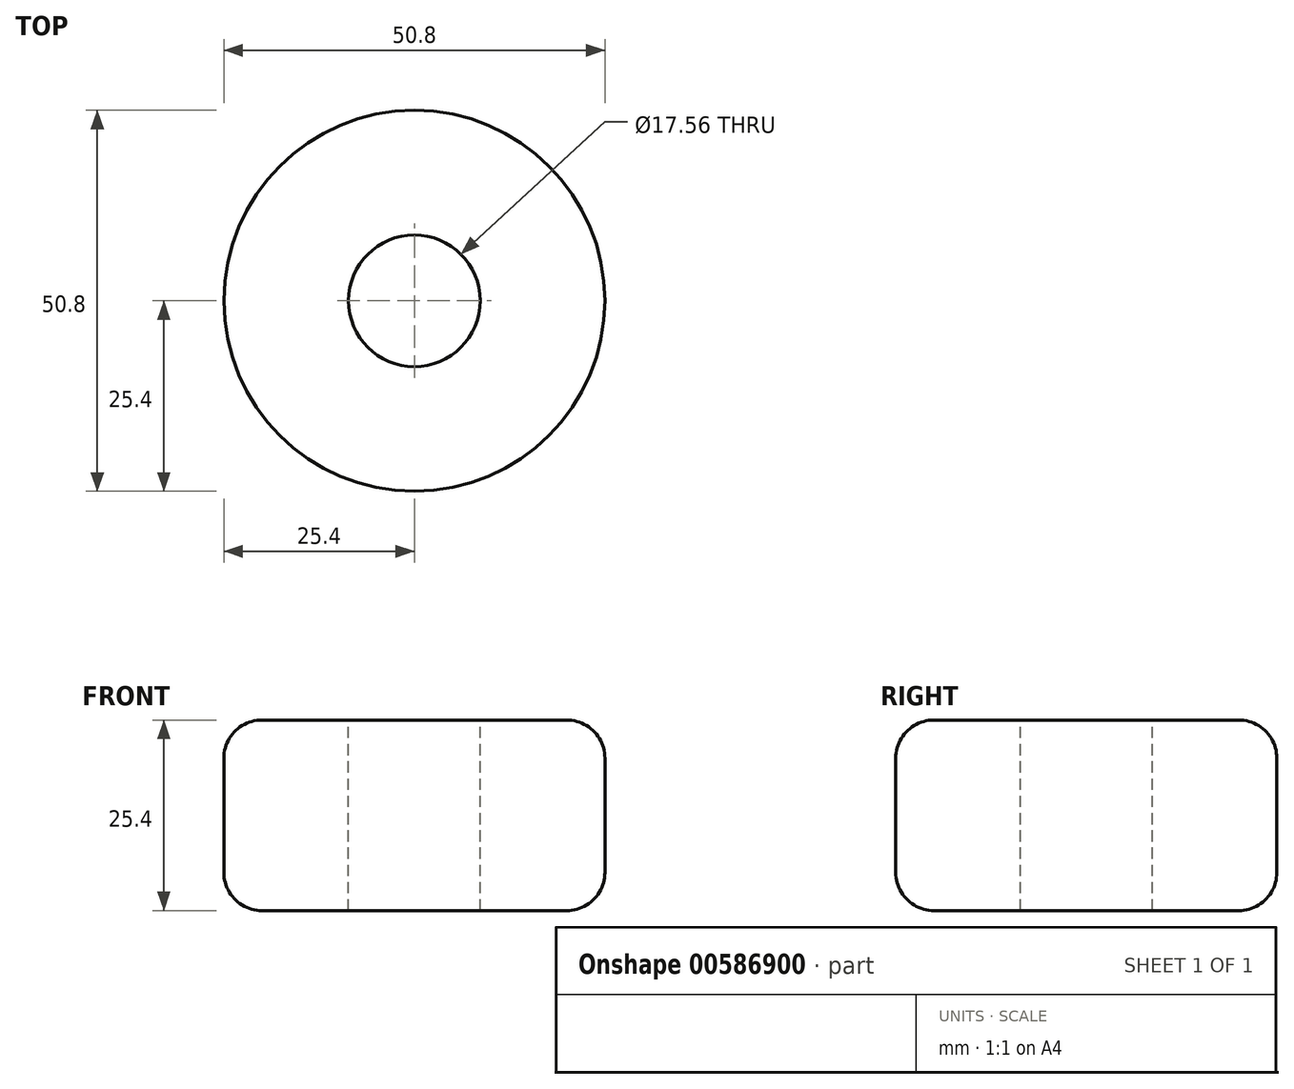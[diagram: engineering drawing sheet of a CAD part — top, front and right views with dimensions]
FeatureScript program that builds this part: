
annotation { "Feature Type Name" : "Feature", "Feature Type Description" : "" }
export const myFeature = defineFeature(function(context is Context, id is Id, definition is map)
    precondition{}
    {
        {
            var Q0;
            Q0=qCreatedBy(makeId("Top.planeOp"),FACE);
            var sketch = newSketch(context, id + "F0", { "sketchPlane" : qUnion([Q0])});
            skCircle(sketch, "E0", {"center": v(0, 0) * mm, "radius": 25.4 * mm});
            skSolve(sketch);
        }
        {
            var Q0;
            Q0=makeQuery(id+"F0.imprint","IMPRINT",FACE,{"disambiguationData":[TD([[makeQuery(id+"F0.imprint","IMPRINT",EDGE,{"derivedFrom":sQuery(id+"F0.wireOp",EDGE,"E0")}),1.0]])]});
            extrude(context, id + "F1", {"entities" : qUnion([Q0]), "depth" : 25.4 * mm, "offsetDistance" : 25.4 * mm});
        }
        {
            var Q0;
            Q0=makeQuery(id+"F1.opExtrude","CAP_FACE",FACE,{"disambiguationData":[OSD([sQuery(id+"F0.wireOp",EDGE,"E0")])],"isStart":false});
            var sketch = newSketch(context, id + "F2", { "sketchPlane" : qUnion([Q0])});
            skCircle(sketch, "E1", {"center": v(0, 0) * mm, "radius": 8.78 * mm});
            skSolve(sketch);
        }
        {
            var Q0;
            Q0=makeQuery(id+"F2.imprint","IMPRINT",FACE,{"disambiguationData":[TD([[makeQuery(id+"F2.imprint","IMPRINT",EDGE,{"derivedFrom":sQuery(id+"F2.wireOp",EDGE,"E1")}),1.0]])]});
            extrude(context, id + "F3", {"entities" : qUnion([Q0]), "operationType" : NewBodyOperationType.REMOVE, "oppositeDirection" : true, "depth" : 25.4 * mm, "offsetDistance" : 25.4 * mm});
        }
        {
            var Q0;
            Q0=makeQuery(id+"F1.opExtrude","CAP_EDGE",EDGE,{"disambiguationData":[OSD([sQuery(id+"F0.wireOp",EDGE,"E0")])],"isStart":false});
            fillet(context, id + "F4", {"entities" : qUnion([Q0]), "radius" : 5.08 * mm, "tangentPropagation" : true, "allowEdgeOverflow" : false});
        }
        {
            var Q0;
            Q0=makeQuery(id+"F1.opExtrude","CAP_EDGE",EDGE,{"disambiguationData":[OSD([sQuery(id+"F0.wireOp",EDGE,"E0")])],"isStart":true});
            fillet(context, id + "F5", {"entities" : qUnion([Q0]), "radius" : 5.08 * mm, "tangentPropagation" : true, "allowEdgeOverflow" : false});
        }
    });
